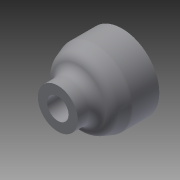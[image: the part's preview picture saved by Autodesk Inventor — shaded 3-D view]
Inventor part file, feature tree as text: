
AUTODESK INVENTOR PART (.ipt)
format: ipt  version: 2015 (Build 190159000, 159)  size: 143,872 bytes
history: native  units: in
note: dims shown in document units (in); Inventor stores cm internally (conversion verified against a paired STEP export)
features: extrude x4, sketch x4, fillet x1
ambient origin geometry x8: Origin, YZ Plane, XZ Plane, XY Plane, X Axis, Y Axis, Z Axis, Center Point
bodies: Solid1 (feature_tree)
feature tree (9):
  extrude  "Extrusion1"  Depth=0.3125in
  extrude  "Extrusion3"  Depth=0.25in
  extrude  "Extrusion4"  Depth=0.125in
  extrude  "Extrusion5"  [1 undecoded]
  fillet  "Fillet1"  [1 undecoded]
  sketch  "Sketch1"  dims[d0=0.3125in d1=0.0in d4=0.1875in d5=-0.1374in]
  sketch  "Sketch3"  dims[d6=0.25in d7=0.0in d8=0.25in]
  sketch  "Sketch4"  dims[d9=0.375in d10=0.0in d11=0.125in]
  sketch  "Sketch5"
note: 2 required parameter values undecoded (feature->parameter linkage not recoverable at this tier; creation-order binding heuristic only, values carry confidence <= 0.55)
